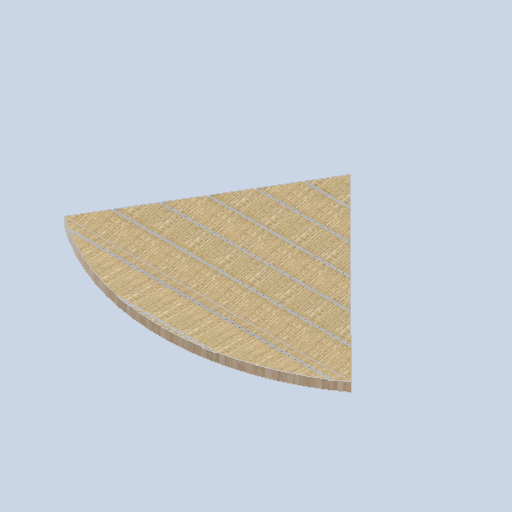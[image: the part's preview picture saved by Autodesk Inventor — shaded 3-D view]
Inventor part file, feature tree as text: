
AUTODESK INVENTOR PART (.ipt)
format: ipt  version: 2024.2 (Build 282272000, 272)  size: 273,408 bytes
history: native  units: in
note: dims shown in document units (in); Inventor stores cm internally (conversion verified against a paired STEP export)
features: sketch x11, plane x4, other x3
ambient origin geometry x8: Origin, YZ Plane, XZ Plane, XY Plane, X Axis, Y Axis, Z Axis, Center Point
bodies: Solid1 (feature_tree)
feature tree (18):
  other  "eave_panel_corner.ipt"
  other  "Solid1::eave_panel_corner.ipt"
  other  "TaggingFeature1"
  sketch  "Sketch1"  dims[d0=0.3937in]
  sketch  "Sketch2"
  sketch  "Sketch5"
  sketch  "Sketch6"
  sketch  "Sketch11"
  sketch  "Sketch12"
  sketch  "Sketch13"
  sketch  "Sketch14"
  sketch  "Sketch15"
  sketch  "Sketch16"
  sketch  "Sketch17"
  plane  "Work Plane1"
  plane  "Work Plane2"
  plane  "Work Plane3"
  plane  "Work Plane4"
